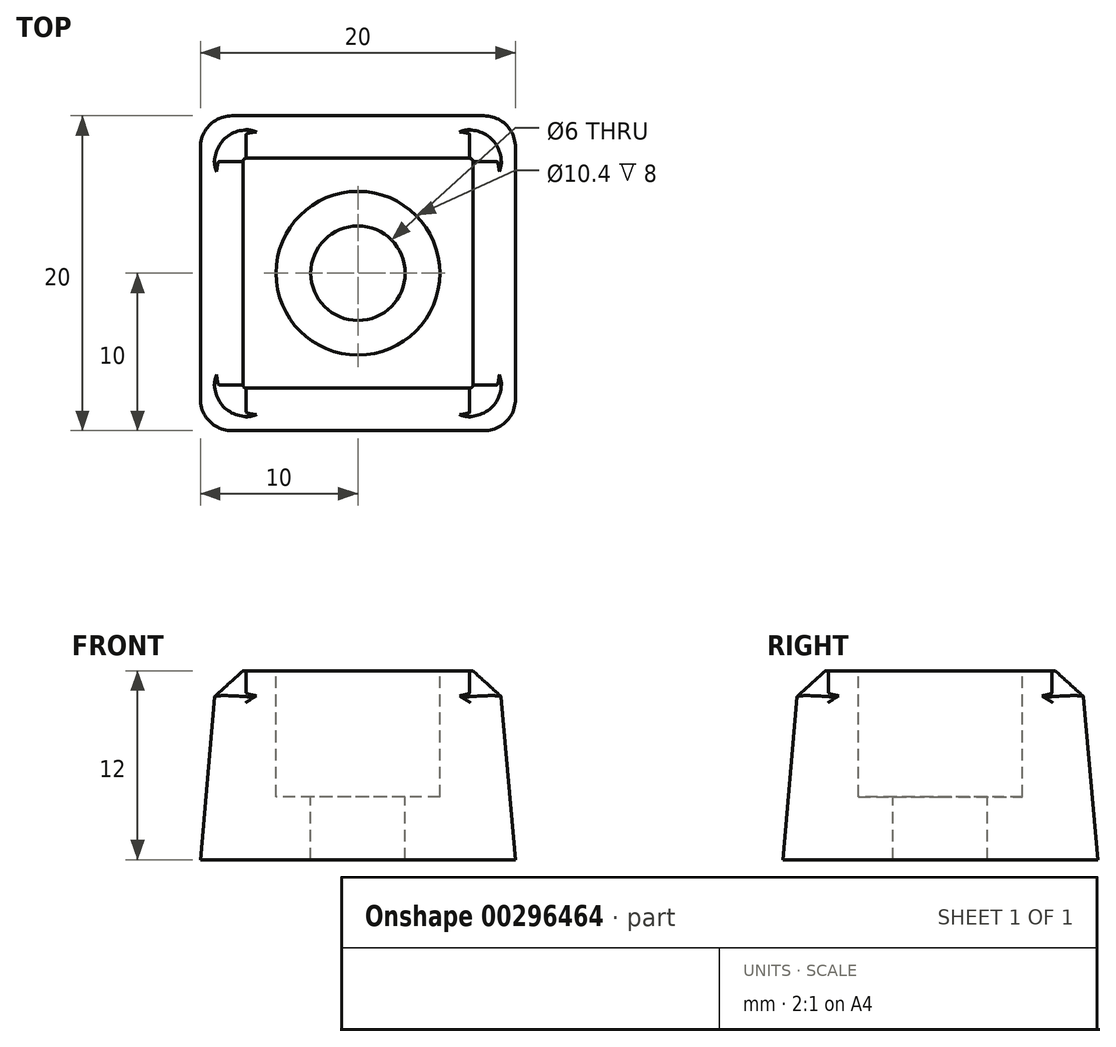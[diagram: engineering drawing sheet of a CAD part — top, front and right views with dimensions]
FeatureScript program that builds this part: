
annotation { "Feature Type Name" : "Feature", "Feature Type Description" : "" }
export const myFeature = defineFeature(function(context is Context, id is Id, definition is map)
    precondition{}
    {
        {
            var Q0;
            Q0=qCreatedBy(makeId("Top.planeOp"),FACE);
            var sketch = newSketch(context, id + "F0", { "sketchPlane" : qUnion([Q0])});
            skLineSegment(sketch, "E0.bottom", {"start": v(9, -10) * mm, "end": v(-9, -10) * mm});
            skLineSegment(sketch, "E0.top", {"start": v(9, 10) * mm, "end": v(-9, 10) * mm});
            skLineSegment(sketch, "E0.left", {"start": v(10, -9) * mm, "end": v(10, 9) * mm});
            skLineSegment(sketch, "E0.right", {"start": v(-10, -9) * mm, "end": v(-10, 9) * mm});
            skPoint(sketch, "E0.middle", {"position": v(0, 0) * mm});
            skPoint(sketch, "E1.visualSharp", {"position": v(10, 10) * mm});
            skArc(sketch, "E1.filletArc", {"start": v(10, 9) * mm, "mid": v(9.7, 9.7) * mm, "end": v(9, 10) * mm});
            skPoint(sketch, "E2.visualSharp", {"position": v(-10, 10) * mm});
            skArc(sketch, "E2.filletArc", {"start": v(-9, 10) * mm, "mid": v(-9.7, 9.7) * mm, "end": v(-10, 9) * mm});
            skPoint(sketch, "E3.visualSharp", {"position": v(-10, -10) * mm});
            skArc(sketch, "E3.filletArc", {"start": v(-10, -9) * mm, "mid": v(-9.7, -9.7) * mm, "end": v(-9, -10) * mm});
            skPoint(sketch, "E4.visualSharp", {"position": v(10, -10) * mm});
            skArc(sketch, "E4.filletArc", {"start": v(9, -10) * mm, "mid": v(9.7, -9.7) * mm, "end": v(10, -9) * mm});
            skSolve(sketch);
        }
        {
            var Q0;
            Q0=makeQuery(id+"F0.imprint","IMPRINT",FACE,{"disambiguationData":[TD([[makeQuery(id+"F0.imprint","IMPRINT",EDGE,{"derivedFrom":sQuery(id+"F0.wireOp",EDGE,"E0.bottom")}),-1.0]])]});
            var Q1;
            Q1=sQuery(id+"F0.wireOp",EDGE,"E1.filletArc");
            extrude(context, id + "F1", {"entities" : qUnion([Q0]), "surfaceEntities" : qUnion([Q1]), "depth" : 12 * mm, "hasDraft" : true, "draftAngle" : 5 * degree, "draftPullDirection" : true});
        }
        {
            var Q0;
            {var subQ0=sQuery(id+"F0.wireOp",EDGE,"E2.filletArc");Q0=makeQuery(id+"F1.*.draft.opDraft","MERGE",EDGE,{"derivedFrom":[makeQuery(id+"F1.opExtrude","SWEPT_EDGE",EDGE,{"disambiguationData":[OSD([sQuery(id+"F0.wireOp",EDGE,"E0.top"),subQ0])]}),makeQuery(id+"F1.opExtrude","SWEPT_EDGE",EDGE,{"disambiguationData":[OSD([sQuery(id+"F0.wireOp",EDGE,"E0.right"),subQ0])]})]});}
            var Q1;
            {var subQ0=sQuery(id+"F0.wireOp",EDGE,"E3.filletArc");Q1=makeQuery(id+"F1.*.draft.opDraft","MERGE",EDGE,{"derivedFrom":[makeQuery(id+"F1.opExtrude","SWEPT_EDGE",EDGE,{"disambiguationData":[OSD([sQuery(id+"F0.wireOp",EDGE,"E0.bottom"),subQ0])]}),makeQuery(id+"F1.opExtrude","SWEPT_EDGE",EDGE,{"disambiguationData":[OSD([sQuery(id+"F0.wireOp",EDGE,"E0.right"),subQ0])]})]});}
            var Q2;
            {var subQ0=sQuery(id+"F0.wireOp",EDGE,"E4.filletArc");Q2=makeQuery(id+"F1.*.draft.opDraft","MERGE",EDGE,{"derivedFrom":[makeQuery(id+"F1.opExtrude","SWEPT_EDGE",EDGE,{"disambiguationData":[OSD([sQuery(id+"F0.wireOp",EDGE,"E0.bottom"),subQ0])]}),makeQuery(id+"F1.opExtrude","SWEPT_EDGE",EDGE,{"disambiguationData":[OSD([sQuery(id+"F0.wireOp",EDGE,"E0.left"),subQ0])]})]});}
            var Q3;
            {var subQ0=sQuery(id+"F0.wireOp",EDGE,"E1.filletArc");Q3=makeQuery(id+"F1.*.draft.opDraft","MERGE",EDGE,{"derivedFrom":[makeQuery(id+"F1.opExtrude","SWEPT_EDGE",EDGE,{"disambiguationData":[OSD([sQuery(id+"F0.wireOp",EDGE,"E0.top"),subQ0])]}),makeQuery(id+"F1.opExtrude","SWEPT_EDGE",EDGE,{"disambiguationData":[OSD([sQuery(id+"F0.wireOp",EDGE,"E0.left"),subQ0])]})]});}
            fillet(context, id + "F2", {"entities" : qUnion([Q0, Q1, Q2, Q3]), "radius" : 2 * mm, "tangentPropagation" : true, "allowEdgeOverflow" : false});
        }
        {
            var Q0;
            Q0=makeQuery(id+"F1.opExtrude","CAP_EDGE",EDGE,{"disambiguationData":[OSD([sQuery(id+"F0.wireOp",EDGE,"E0.bottom")])],"isStart":false});
            chamfer(context, id + "F3", {"entities" : qUnion([Q0]), "width" : 1.8 * mm, "tangentPropagation" : true});
        }
        {
            var Q0;
            Q0=makeQuery(id+"F1.opExtrude","CAP_FACE",FACE,{"disambiguationData":[OSD([sQuery(id+"F0.wireOp",EDGE,"E0.bottom"),sQuery(id+"F0.wireOp",EDGE,"E0.top"),sQuery(id+"F0.wireOp",EDGE,"E0.left"),sQuery(id+"F0.wireOp",EDGE,"E0.right"),sQuery(id+"F0.wireOp",EDGE,"E1.filletArc"),sQuery(id+"F0.wireOp",EDGE,"E2.filletArc"),sQuery(id+"F0.wireOp",EDGE,"E3.filletArc"),sQuery(id+"F0.wireOp",EDGE,"E4.filletArc")])],"isStart":false});
            var sketch = newSketch(context, id + "F4", { "sketchPlane" : qUnion([Q0])});
            skCircle(sketch, "E5", {"center": v(0, 0) * mm, "radius": 3 * mm});
            skCircle(sketch, "E6", {"center": v(0, 0) * mm, "radius": 5.2 * mm});
            skSolve(sketch);
        }
        {
            var Q0;
            Q0=makeQuery(id+"F4.imprint","IMPRINT",FACE,{"disambiguationData":[TD([[makeQuery(id+"F4.imprint","IMPRINT",EDGE,{"derivedFrom":sQuery(id+"F4.wireOp",EDGE,"E5")}),1.0]])]});
            extrude(context, id + "F5", {"entities" : qUnion([Q0]), "operationType" : NewBodyOperationType.REMOVE, "endBound" : BoundingType.THROUGH_ALL, "oppositeDirection" : true, "depth" : 8 * mm});
        }
        {
            var Q0;
            Q0=makeQuery(id+"F4.imprint","IMPRINT",FACE,{"disambiguationData":[TD([[makeQuery(id+"F4.imprint","IMPRINT",EDGE,{"derivedFrom":sQuery(id+"F4.wireOp",EDGE,"E5")}),-1.0]])]});
            extrude(context, id + "F6", {"entities" : qUnion([Q0]), "operationType" : NewBodyOperationType.REMOVE, "oppositeDirection" : true, "depth" : 8 * mm});
        }
        {
            var Q0;
            {var subQ0=sQuery(id+"F0.wireOp",EDGE,"E0.bottom");Q0=makeQuery(id+"F3.opChamfer","BLEND_EDGE",EDGE,{"blendedFrom":[makeQuery(id+"F1.opExtrude","CAP_EDGE",EDGE,{"disambiguationData":[OSD([subQ0])],"isStart":false}),makeQuery(id+"F1.opExtrude","SWEPT_FACE",FACE,{"disambiguationData":[OSD([subQ0])]})],"blendedInto":[makeQuery(id+"F1.opExtrude","SWEPT_FACE",FACE,{"disambiguationData":[OSD([subQ0])]})]});}
            var Q1;
            {var subQ0=sQuery(id+"F0.wireOp",EDGE,"E0.left");Q1=makeQuery(id+"F3.opChamfer","BLEND_EDGE",EDGE,{"blendedFrom":[makeQuery(id+"F1.opExtrude","CAP_EDGE",EDGE,{"disambiguationData":[OSD([subQ0])],"isStart":false}),makeQuery(id+"F1.opExtrude","SWEPT_FACE",FACE,{"disambiguationData":[OSD([subQ0])]})],"blendedInto":[makeQuery(id+"F1.opExtrude","SWEPT_FACE",FACE,{"disambiguationData":[OSD([subQ0])]})]});}
            var Q2;
            {var subQ0=sQuery(id+"F0.wireOp",EDGE,"E0.right");Q2=makeQuery(id+"F3.opChamfer","BLEND_EDGE",EDGE,{"blendedFrom":[makeQuery(id+"F1.opExtrude","CAP_EDGE",EDGE,{"disambiguationData":[OSD([subQ0])],"isStart":false}),makeQuery(id+"F1.opExtrude","SWEPT_FACE",FACE,{"disambiguationData":[OSD([subQ0])]})],"blendedInto":[makeQuery(id+"F1.opExtrude","SWEPT_FACE",FACE,{"disambiguationData":[OSD([subQ0])]})]});}
            var Q3;
            {var subQ0=sQuery(id+"F0.wireOp",EDGE,"E0.bottom");Q3=makeQuery(id+"F3.opChamfer","BLEND_EDGE",EDGE,{"blendedFrom":[makeQuery(id+"F1.opExtrude","CAP_EDGE",EDGE,{"disambiguationData":[OSD([subQ0])],"isStart":false}),makeQuery(id+"F2.opFillet","BLEND_FACE",FACE,{"disambiguationData":[OSD([subQ0,sQuery(id+"F0.wireOp",EDGE,"E0.right"),sQuery(id+"F0.wireOp",EDGE,"E3.filletArc")])]})],"blendedInto":[makeQuery(id+"F2.opFillet","BLEND_FACE",FACE,{"disambiguationData":[OSD([subQ0,sQuery(id+"F0.wireOp",EDGE,"E0.right"),sQuery(id+"F0.wireOp",EDGE,"E3.filletArc")])]})]});}
            var Q4;
            {var subQ0=sQuery(id+"F0.wireOp",EDGE,"E0.left");Q4=makeQuery(id+"F3.opChamfer","BLEND_EDGE",EDGE,{"blendedFrom":[makeQuery(id+"F1.opExtrude","CAP_EDGE",EDGE,{"disambiguationData":[OSD([subQ0])],"isStart":false}),makeQuery(id+"F2.opFillet","BLEND_FACE",FACE,{"disambiguationData":[OSD([sQuery(id+"F0.wireOp",EDGE,"E0.bottom"),subQ0,sQuery(id+"F0.wireOp",EDGE,"E4.filletArc")])]})],"blendedInto":[makeQuery(id+"F2.opFillet","BLEND_FACE",FACE,{"disambiguationData":[OSD([sQuery(id+"F0.wireOp",EDGE,"E0.bottom"),subQ0,sQuery(id+"F0.wireOp",EDGE,"E4.filletArc")])]})]});}
            var Q5;
            {var subQ0=sQuery(id+"F0.wireOp",EDGE,"E0.top");Q5=makeQuery(id+"F3.opChamfer","BLEND_EDGE",EDGE,{"blendedFrom":[makeQuery(id+"F1.opExtrude","CAP_EDGE",EDGE,{"disambiguationData":[OSD([subQ0])],"isStart":false}),makeQuery(id+"F2.opFillet","BLEND_FACE",FACE,{"disambiguationData":[OSD([subQ0,sQuery(id+"F0.wireOp",EDGE,"E0.left"),sQuery(id+"F0.wireOp",EDGE,"E1.filletArc")])]})],"blendedInto":[makeQuery(id+"F2.opFillet","BLEND_FACE",FACE,{"disambiguationData":[OSD([subQ0,sQuery(id+"F0.wireOp",EDGE,"E0.left"),sQuery(id+"F0.wireOp",EDGE,"E1.filletArc")])]})]});}
            var Q6;
            {var subQ0=sQuery(id+"F0.wireOp",EDGE,"E0.top");Q6=makeQuery(id+"F3.opChamfer","BLEND_EDGE",EDGE,{"blendedFrom":[makeQuery(id+"F1.opExtrude","CAP_EDGE",EDGE,{"disambiguationData":[OSD([subQ0])],"isStart":false}),makeQuery(id+"F1.opExtrude","SWEPT_FACE",FACE,{"disambiguationData":[OSD([subQ0])]})],"blendedInto":[makeQuery(id+"F1.opExtrude","SWEPT_FACE",FACE,{"disambiguationData":[OSD([subQ0])]})]});}
            var Q7;
            {var subQ0=sQuery(id+"F0.wireOp",EDGE,"E0.right");Q7=makeQuery(id+"F3.opChamfer","BLEND_EDGE",EDGE,{"blendedFrom":[makeQuery(id+"F1.opExtrude","CAP_EDGE",EDGE,{"disambiguationData":[OSD([subQ0])],"isStart":false}),makeQuery(id+"F2.opFillet","BLEND_FACE",FACE,{"disambiguationData":[OSD([sQuery(id+"F0.wireOp",EDGE,"E0.top"),subQ0,sQuery(id+"F0.wireOp",EDGE,"E2.filletArc")])]})],"blendedInto":[makeQuery(id+"F2.opFillet","BLEND_FACE",FACE,{"disambiguationData":[OSD([sQuery(id+"F0.wireOp",EDGE,"E0.top"),subQ0,sQuery(id+"F0.wireOp",EDGE,"E2.filletArc")])]})]});}
            fillet(context, id + "F7", {"entities" : qUnion([Q0, Q1, Q2, Q3, Q4, Q5, Q6, Q7]), "radius" : 1 * mm, "tangentPropagation" : true, "allowEdgeOverflow" : false});
        }
    });
